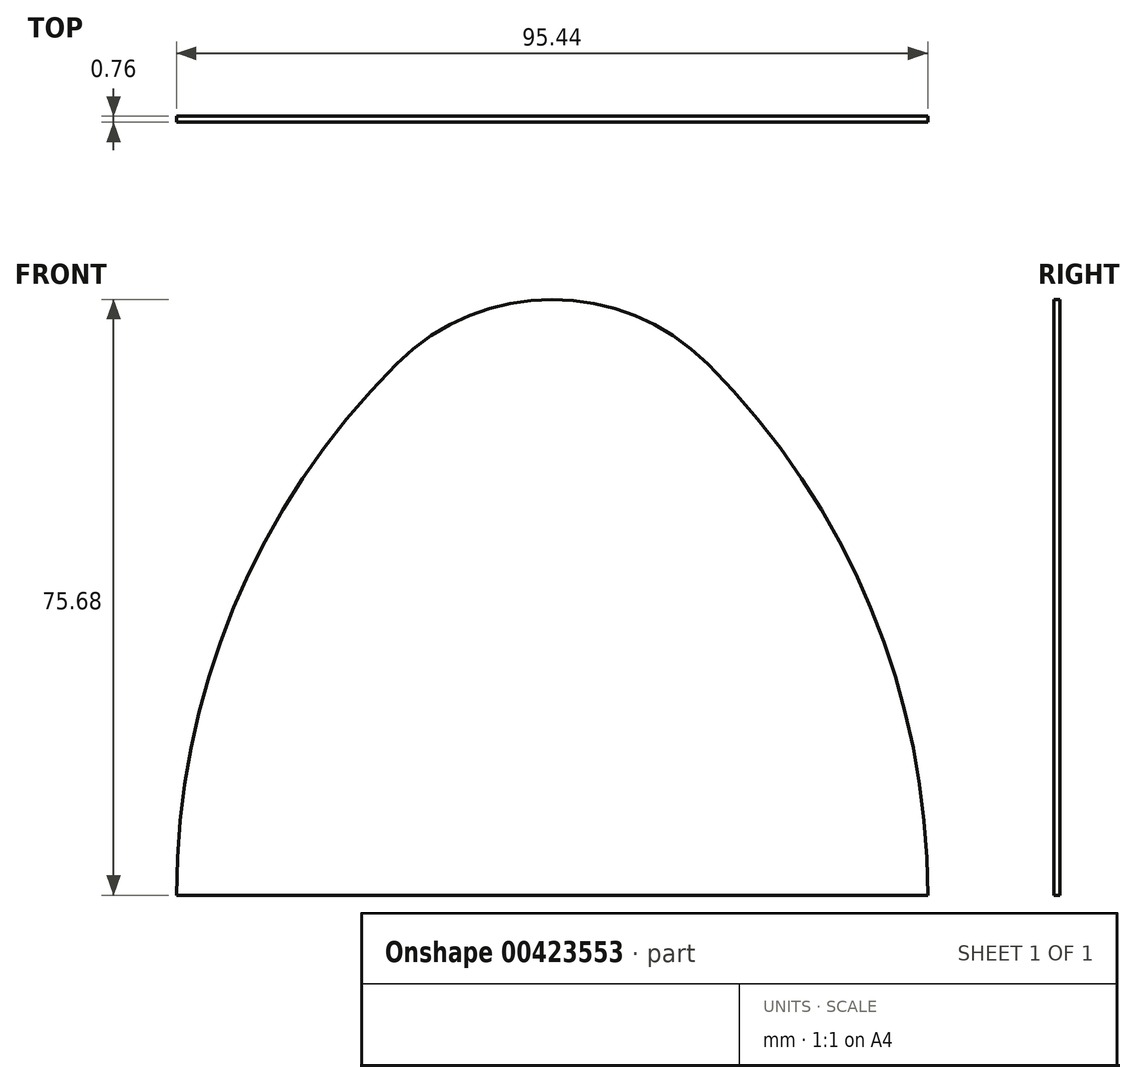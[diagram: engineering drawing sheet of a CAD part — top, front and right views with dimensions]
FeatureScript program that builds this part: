
annotation { "Feature Type Name" : "Feature", "Feature Type Description" : "" }
export const myFeature = defineFeature(function(context is Context, id is Id, definition is map)
    precondition{}
    {
        {
            var Q0;
            Q0=qCreatedBy(makeId("Front.planeOp"),FACE);
            var sketch = newSketch(context, id + "F0", { "sketchPlane" : qUnion([Q0])});
            skArc(sketch, "E0", {"start": v(-47.72, 0) * mm, "mid": v(0, -47.72) * mm, "end": v(47.72, 0) * mm});
            skLineSegment(sketch, "E1", {"start": v(-47.72, 0) * mm, "end": v(47.72, 0) * mm});
            skArc(sketch, "E2", {"start": v(47.72, 0) * mm, "mid": v(40.46, 36.52) * mm, "end": v(19.77, 67.49) * mm});
            skArc(sketch, "E3", {"start": v(-19.77, 67.49) * mm, "mid": v(-40.46, 36.52) * mm, "end": v(-47.72, 0) * mm});
            skArc(sketch, "E4", {"start": v(19.77, 67.49) * mm, "mid": v(0, 75.68) * mm, "end": v(-19.77, 67.49) * mm});
            skSolve(sketch);
        }
        {
            var Q0;
            Q0=qCreatedBy(makeId("Front.planeOp"),FACE);
            var sketch = newSketch(context, id + "F1", { "sketchPlane" : qUnion([Q0])});
            skSolve(sketch);
        }
        {
            var Q0;
            Q0 = qSketchRegion(id + "F1", true);
            var Q1;
            Q1=makeQuery(id+"F0.imprint","IMPRINT",FACE,{"disambiguationData":[TD([[makeQuery(id+"F0.imprint","IMPRINT",EDGE,{"derivedFrom":sQuery(id+"F0.wireOp",EDGE,"E1")}),1.0]])]});
            extrude(context, id + "F2", {"entities" : qUnion([Q0, Q1]), "depth" : 0.76 * mm});
        }
    });
